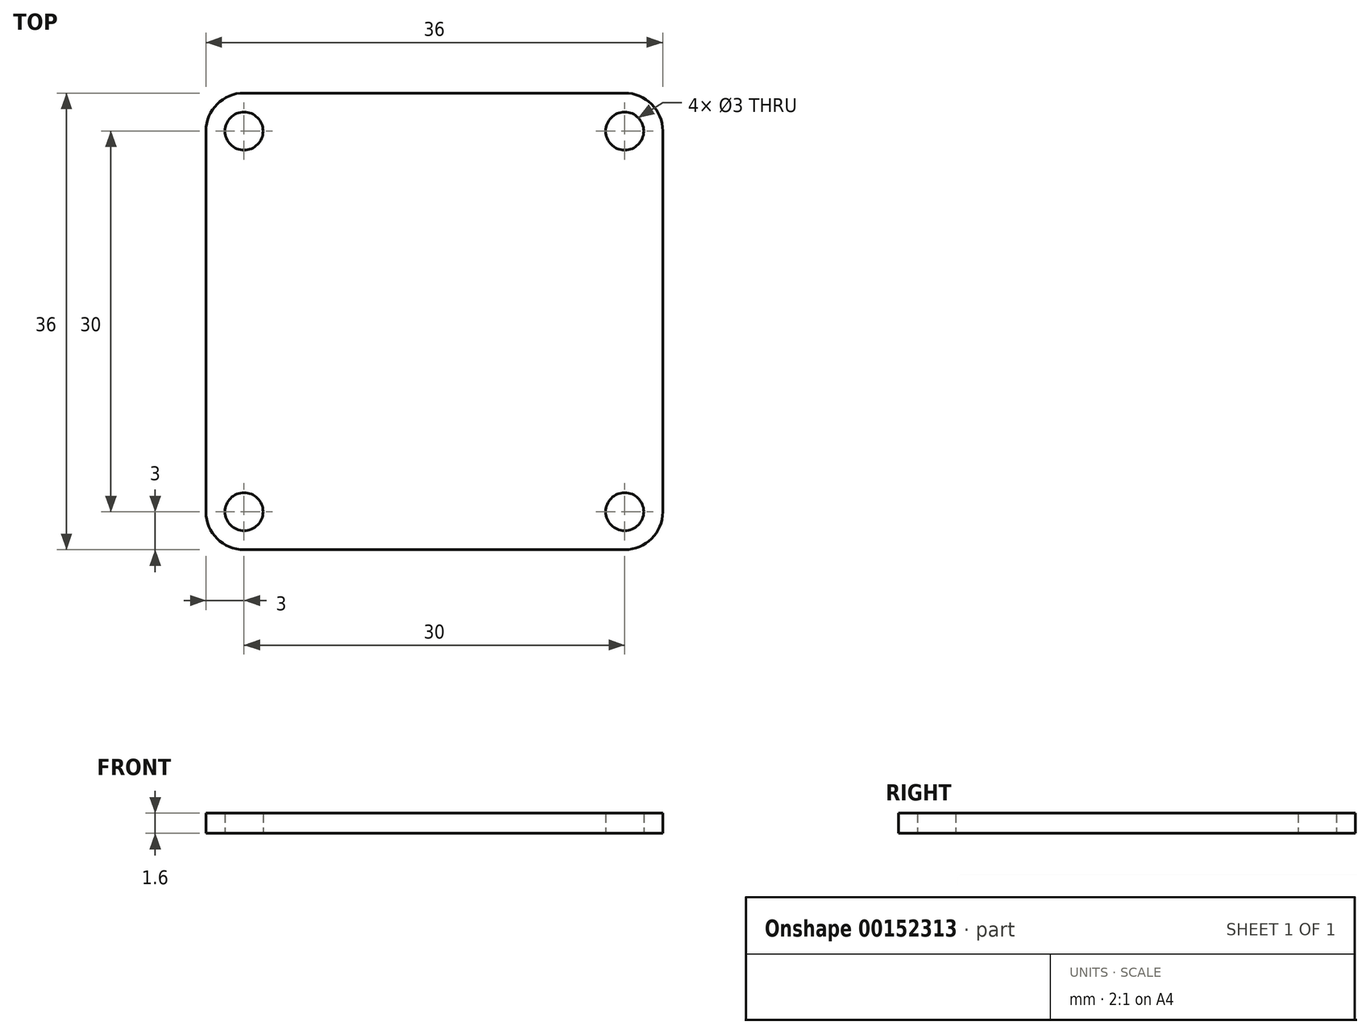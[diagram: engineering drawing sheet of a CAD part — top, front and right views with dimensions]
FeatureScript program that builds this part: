
annotation { "Feature Type Name" : "Feature", "Feature Type Description" : "" }
export const myFeature = defineFeature(function(context is Context, id is Id, definition is map)
    precondition{}
    {
        {
            var Q0;
            Q0=qCreatedBy(makeId("Top.planeOp"),FACE);
            var sketch = newSketch(context, id + "F0", { "sketchPlane" : qUnion([Q0])});
            skLineSegment(sketch, "E0.bottom", {"start": v(18, 18) * mm, "end": v(-18, 18) * mm});
            skLineSegment(sketch, "E0.top", {"start": v(18, -18) * mm, "end": v(-18, -18) * mm});
            skLineSegment(sketch, "E0.left", {"start": v(18, 18) * mm, "end": v(18, -18) * mm});
            skLineSegment(sketch, "E0.right", {"start": v(-18, 18) * mm, "end": v(-18, -18) * mm});
            skPoint(sketch, "E0.middle", {"position": v(0, 0) * mm});
            skLineSegment(sketch, "E1", {"start": v(0, 18) * mm, "end": v(0, -18) * mm, "construction": true});
            skLineSegment(sketch, "E2", {"start": v(-18, 0) * mm, "end": v(18, 0) * mm, "construction": true});
            skCircle(sketch, "E3", {"center": v(-15, 15) * mm, "radius": 1.5 * mm});
            skCircle(sketch, "E4.MirrorC", {"center": v(15, 15) * mm, "radius": 1.5 * mm});
            skLineSegment(sketch, "E5.MirrorCS", {"start": v(18, 0) * mm, "end": v(-18, 0) * mm, "construction": true});
            skCircle(sketch, "E6.MirrorC", {"center": v(-15, -15) * mm, "radius": 1.5 * mm});
            skCircle(sketch, "E7.MirrorC", {"center": v(15, -15) * mm, "radius": 1.5 * mm});
            skSolve(sketch);
        }
        {
            var Q0;
            Q0 = qSketchRegion(id + "F0", true);
            extrude(context, id + "F1", {"entities" : qUnion([Q0]), "depth" : 1.6 * mm});
        }
        {
            var Q0;
            Q0=makeQuery(id+"F1.opExtrude","SWEPT_EDGE",EDGE,{"disambiguationData":[OSD([sQuery(id+"F0.wireOp",EDGE,"E0.bottom"),sQuery(id+"F0.wireOp",EDGE,"E0.right")])]});
            var Q1;
            Q1=makeQuery(id+"F1.opExtrude","SWEPT_EDGE",EDGE,{"disambiguationData":[OSD([sQuery(id+"F0.wireOp",EDGE,"E0.bottom"),sQuery(id+"F0.wireOp",EDGE,"E0.left")])]});
            var Q2;
            Q2=makeQuery(id+"F1.opExtrude","SWEPT_EDGE",EDGE,{"disambiguationData":[OSD([sQuery(id+"F0.wireOp",EDGE,"E0.top"),sQuery(id+"F0.wireOp",EDGE,"E0.left")])]});
            var Q3;
            Q3=makeQuery(id+"F1.opExtrude","SWEPT_EDGE",EDGE,{"disambiguationData":[OSD([sQuery(id+"F0.wireOp",EDGE,"E0.top"),sQuery(id+"F0.wireOp",EDGE,"E0.right")])]});
            fillet(context, id + "F2", {"entities" : qUnion([Q0, Q1, Q2, Q3]), "radius" : 3 * mm, "tangentPropagation" : true, "allowEdgeOverflow" : false});
        }
    });
